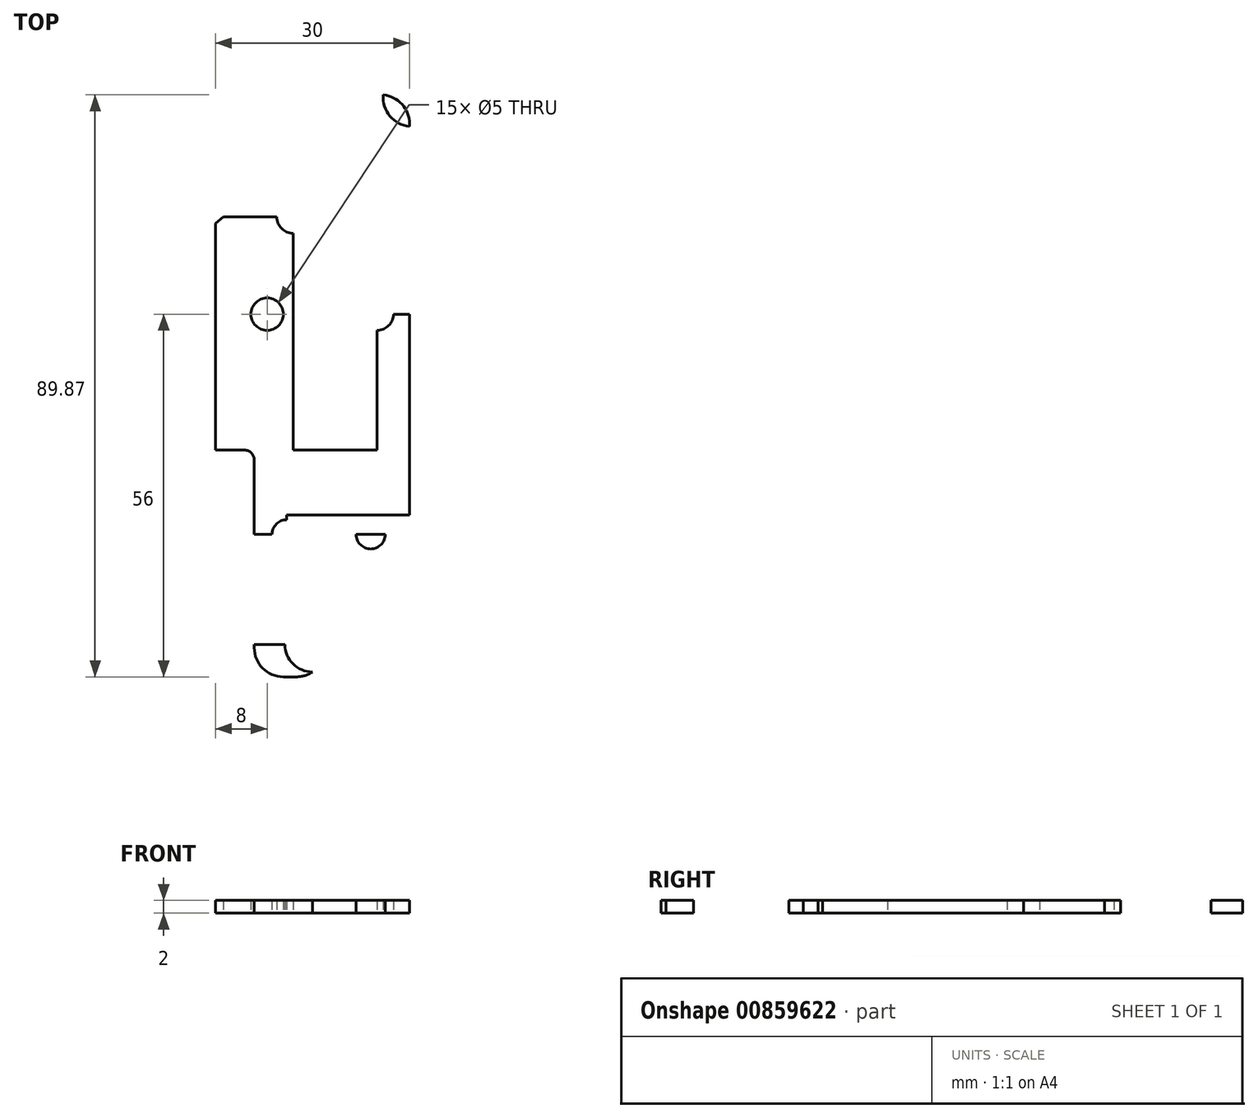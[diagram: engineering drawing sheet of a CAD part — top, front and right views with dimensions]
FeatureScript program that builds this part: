
annotation { "Feature Type Name" : "Feature", "Feature Type Description" : "" }
export const myFeature = defineFeature(function(context is Context, id is Id, definition is map)
    precondition{}
    {
        {
            var Q0;
            Q0=qCreatedBy(makeId("Top.planeOp"),FACE);
            var sketch = newSketch(context, id + "F0", { "sketchPlane" : qUnion([Q0])});
            skLineSegment(sketch, "E0.bottom", {"start": v(12, -12.5) * mm, "end": v(12, 12.5) * mm});
            skLineSegment(sketch, "E0.top", {"start": v(-12, -12.5) * mm, "end": v(-12, 12.5) * mm});
            skLineSegment(sketch, "E0.left", {"start": v(12, -12.5) * mm, "end": v(-12, -12.5) * mm});
            skLineSegment(sketch, "E0.right", {"start": v(12, 12.5) * mm, "end": v(-12, 12.5) * mm});
            skPoint(sketch, "E0.middle", {"position": v(0, 0) * mm});
            skLineSegment(sketch, "E1.bottom", {"start": v(12, 12.5) * mm, "end": v(12, 22.5) * mm});
            skLineSegment(sketch, "E1.top", {"start": v(-12, 12.5) * mm, "end": v(-12, 22.5) * mm});
            skLineSegment(sketch, "E1.right", {"start": v(12, 22.5) * mm, "end": v(-12, 22.5) * mm});
            skLineSegment(sketch, "E2.bottom", {"start": v(12, 22.5) * mm, "end": v(12, 72.5) * mm});
            skLineSegment(sketch, "E2.top", {"start": v(-18, 22.5) * mm, "end": v(-18, 72.5) * mm});
            skLineSegment(sketch, "E2.left", {"start": v(12, 22.5) * mm, "end": v(-18, 22.5) * mm});
            skLineSegment(sketch, "E2.right", {"start": v(12, 72.5) * mm, "end": v(-18, 72.5) * mm});
            skLineSegment(sketch, "E3", {"start": v(-18, 22.5) * mm, "end": v(-18, 57.5) * mm});
            skLineSegment(sketch, "E4", {"start": v(12, 72.5) * mm, "end": v(12, 82.5) * mm});
            skLineSegment(sketch, "E5", {"start": v(12, 82.5) * mm, "end": v(-18, 57.5) * mm});
            skLineSegment(sketch, "E6.bottom", {"start": v(12, 22.5) * mm, "end": v(12, 43.5) * mm});
            skLineSegment(sketch, "E6.top", {"start": v(7, 22.5) * mm, "end": v(7, 43.5) * mm});
            skLineSegment(sketch, "E6.left", {"start": v(12, 22.5) * mm, "end": v(7, 22.5) * mm});
            skLineSegment(sketch, "E6.right", {"start": v(12, 43.5) * mm, "end": v(7, 43.5) * mm});
            skLineSegment(sketch, "E7", {"start": v(7, 43.5) * mm, "end": v(7, 69.5) * mm});
            skCircle(sketch, "E8", {"center": v(7, 69.5) * mm, "radius": 2.5 * mm});
            skCircle(sketch, "E9", {"center": v(7, 43.5) * mm, "radius": 2.5 * mm});
            skLineSegment(sketch, "E10", {"start": v(7, 43.5) * mm, "end": v(-10, 43.5) * mm});
            skCircle(sketch, "E11", {"center": v(-10, 43.5) * mm, "radius": 2.5 * mm});
            skLineSegment(sketch, "E12.bottom", {"start": v(-18, 22.5) * mm, "end": v(-18, 58.5) * mm});
            skLineSegment(sketch, "E12.top", {"start": v(-6, 22.5) * mm, "end": v(-6, 58.5) * mm});
            skLineSegment(sketch, "E12.left", {"start": v(-18, 22.5) * mm, "end": v(-6, 22.5) * mm});
            skLineSegment(sketch, "E12.right", {"start": v(-18, 58.5) * mm, "end": v(-6, 58.5) * mm});
            skCircle(sketch, "E13", {"center": v(-6, 58.5) * mm, "radius": 2.5 * mm});
            skLineSegment(sketch, "E14.bottom", {"start": v(-12, 12.5) * mm, "end": v(-12, 9.5) * mm});
            skLineSegment(sketch, "E14.top", {"start": v(-7, 12.5) * mm, "end": v(-7, 9.5) * mm});
            skLineSegment(sketch, "E14.left", {"start": v(-12, 12.5) * mm, "end": v(-7, 12.5) * mm});
            skLineSegment(sketch, "E14.right", {"start": v(-12, 9.5) * mm, "end": v(-7, 9.5) * mm});
            skCircle(sketch, "E15", {"center": v(-7, 9.5) * mm, "radius": 2.25 * mm});
            skLineSegment(sketch, "E16", {"start": v(12, 9.5) * mm, "end": v(6, 9.5) * mm});
            skCircle(sketch, "E17", {"center": v(6, 9.5) * mm, "radius": 2.25 * mm});
            skLineSegment(sketch, "E18", {"start": v(6, -12.5) * mm, "end": v(6, 1.5) * mm});
            skCircle(sketch, "E19", {"center": v(6, 1.5) * mm, "radius": 3.5 * mm});
            skCircle(sketch, "E20", {"center": v(-7, 1.5) * mm, "radius": 3.5 * mm});
            skPoint(sketch, "E21", {"position": v(-4.75, 9.5) * mm});
            skPoint(sketch, "E22", {"position": v(-9.25, 9.5) * mm});
            skPoint(sketch, "E23", {"position": v(8.25, 9.5) * mm});
            skPoint(sketch, "E24", {"position": v(3.75, 9.5) * mm});
            skLineSegment(sketch, "E25.bottom", {"start": v(8.25, 9.5) * mm, "end": v(8.25, 4.18) * mm});
            skLineSegment(sketch, "E25.top", {"start": v(3.75, 9.5) * mm, "end": v(3.75, 4.18) * mm});
            skLineSegment(sketch, "E25.left", {"start": v(8.25, 9.5) * mm, "end": v(3.75, 9.5) * mm});
            skLineSegment(sketch, "E25.right", {"start": v(8.25, 4.18) * mm, "end": v(3.75, 4.18) * mm});
            skLineSegment(sketch, "E26.bottom", {"start": v(-4.75, 9.5) * mm, "end": v(-4.75, 4.18) * mm});
            skLineSegment(sketch, "E26.top", {"start": v(-9.25, 9.5) * mm, "end": v(-9.25, 4.18) * mm});
            skLineSegment(sketch, "E26.left", {"start": v(-4.75, 9.5) * mm, "end": v(-9.25, 9.5) * mm});
            skLineSegment(sketch, "E26.right", {"start": v(-4.75, 4.18) * mm, "end": v(-9.25, 4.18) * mm});
            skLineSegment(sketch, "E27.bottom", {"start": v(-12, -12.5) * mm, "end": v(-12, -7.5) * mm});
            skLineSegment(sketch, "E27.top", {"start": v(-3, -12.5) * mm, "end": v(-3, -7.5) * mm});
            skLineSegment(sketch, "E27.left", {"start": v(-12, -12.5) * mm, "end": v(-3, -12.5) * mm});
            skLineSegment(sketch, "E27.right", {"start": v(-12, -7.5) * mm, "end": v(-3, -7.5) * mm});
            skCircle(sketch, "E28", {"center": v(-3, -7.5) * mm, "radius": 4.25 * mm});
            skLineSegment(sketch, "E29.bottom", {"start": v(-18, 22.5) * mm, "end": v(-12, 22.5) * mm});
            skLineSegment(sketch, "E29.top", {"start": v(-18, 24) * mm, "end": v(-12, 24) * mm});
            skLineSegment(sketch, "E29.left", {"start": v(-18, 22.5) * mm, "end": v(-18, 24) * mm});
            skLineSegment(sketch, "E29.right", {"start": v(-12, 22.5) * mm, "end": v(-12, 24) * mm});
            skSolve(sketch);
        }
        {
            var Q0;
            {var subQ12=sQuery(id+"F0.wireOp",EDGE,"E2.bottom");Q0=makeQuery(id+"F0.imprint","IMPRINT",FACE,{"disambiguationData":[TD([[makeQuery(id+"F0.imprint","IMPRINT",EDGE,{"derivedFrom":subQ12}),1.0]])]});}
            var Q1;
            Q1=makeQuery(id+"F0.imprint","IMPRINT",FACE,{"disambiguationData":[TD([[makeQuery(id+"F0.imprint","IMPRINT",EDGE,{"derivedFrom":sQuery(id+"F0.wireOp",EDGE,"E11")}),-1.0]])]});
            var Q2;
            {var subQ5=sQuery(id+"F0.wireOp",EDGE,"E2.left");Q2=makeQuery(id+"F0.imprint","IMPRINT",FACE,{"disambiguationData":[TD([[makeQuery(id+"F0.imprint","IMPRINT",EDGE,{"derivedFrom":subQ5}),-1.0]])]});}
            var Q3;
            {var subQ1=sQuery(id+"F0.wireOp",EDGE,"E6.bottom");Q3=makeQuery(id+"F0.imprint","IMPRINT",FACE,{"disambiguationData":[TD([[makeQuery(id+"F0.imprint","IMPRINT",EDGE,{"derivedFrom":subQ1}),1.0]])]});}
            var Q4;
            Q4=makeQuery(id+"F0.imprint","IMPRINT",FACE,{"disambiguationData":[TD([[makeQuery(id+"F0.imprint","IMPRINT",EDGE,{"derivedFrom":sQuery(id+"F0.wireOp",EDGE,"E1.bottom")}),1.0]])]});
            var Q5;
            {var subQ11=sQuery(id+"F0.wireOp",EDGE,"E0.top");Q5=makeQuery(id+"F0.imprint","IMPRINT",FACE,{"disambiguationData":[TD([[makeQuery(id+"F0.imprint","IMPRINT",EDGE,{"derivedFrom":subQ11}),-1.0]])]});}
            var Q6;
            {var subQ0=sQuery(id+"F0.wireOp",EDGE,"E16");Q6=makeQuery(id+"F0.imprint","IMPRINT",FACE,{"disambiguationData":[TD([[makeQuery(id+"F0.imprint","IMPRINT",EDGE,{"derivedFrom":subQ0}),1.0]])]});}
            var Q7;
            {var subQ1=sQuery(id+"F0.wireOp",EDGE,"E27.bottom");Q7=makeQuery(id+"F0.imprint","IMPRINT",FACE,{"disambiguationData":[TD([[makeQuery(id+"F0.imprint","IMPRINT",EDGE,{"derivedFrom":subQ1}),-1.0]])]});}
            var Q8;
            Q8=makeQuery(id+"F0.imprint","IMPRINT",FACE,{"disambiguationData":[TD([[makeQuery(id+"F0.imprint","IMPRINT",EDGE,{"derivedFrom":sQuery(id+"F0.wireOp",EDGE,"E14.bottom")}),1.0]])]});
            var Q9;
            {var subQ0=sQuery(id+"F0.wireOp",EDGE,"E4");Q9=makeQuery(id+"F0.imprint","IMPRINT",FACE,{"disambiguationData":[TD([[makeQuery(id+"F0.imprint","IMPRINT",EDGE,{"derivedFrom":subQ0}),1.0]])]});}
            extrude(context, id + "F1", {"entities" : qUnion([Q0, Q1, Q2, Q3, Q4, Q5, Q6, Q7, Q8, Q9]), "depth" : 2 * mm, "offsetDistance" : 25 * mm});
        }
        {
            var Q0;
            Q0=makeQuery(id+"F1.opExtrude","SWEPT_EDGE",EDGE,{"disambiguationData":[OSD([sQuery(id+"F0.wireOp",EDGE,"E4"),sQuery(id+"F0.wireOp",EDGE,"E5")])]});
            var Q1;
            Q1=makeQuery(id+"F1.opExtrude","SWEPT_EDGE",EDGE,{"disambiguationData":[OSD([sQuery(id+"F0.wireOp",EDGE,"E5"),sQuery(id+"F0.wireOp",EDGE,"E12.bottom")])]});
            var Q2;
            Q2=makeQuery(id+"F1.opExtrude","SWEPT_EDGE",EDGE,{"disambiguationData":[OSD([sQuery(id+"F0.wireOp",EDGE,"E12.bottom"),sQuery(id+"F0.wireOp",EDGE,"E12.left")])]});
            var Q3;
            Q3=makeQuery(id+"F1.opExtrude","SWEPT_EDGE",EDGE,{"disambiguationData":[OSD([sQuery(id+"F0.wireOp",EDGE,"E27.bottom"),sQuery(id+"F0.wireOp",EDGE,"E27.left")])]});
            var Q4;
            Q4=makeQuery(id+"F1.opExtrude","SWEPT_EDGE",EDGE,{"disambiguationData":[OSD([sQuery(id+"F0.wireOp",EDGE,"E0.bottom"),sQuery(id+"F0.wireOp",EDGE,"E0.left")])]});
            var Q5;
            Q5=makeQuery(id+"F1.opExtrude","SWEPT_EDGE",EDGE,{"disambiguationData":[OSD([sQuery(id+"F0.wireOp",EDGE,"E12.bottom"),sQuery(id+"F0.wireOp",EDGE,"E29.top"),sQuery(id+"F0.wireOp",EDGE,"E29.left")])]});
            fillet(context, id + "F2", {"entities" : qUnion([Q0, Q1, Q2, Q3, Q4, Q5]), "radius" : 4.5 * mm, "tangentPropagation" : true, "allowEdgeOverflow" : false});
        }
        {
            var Q0;
            Q0=makeQuery(id+"F1.opExtrude","SWEPT_EDGE",EDGE,{"disambiguationData":[OSD([sQuery(id+"F0.wireOp",EDGE,"E29.top"),sQuery(id+"F0.wireOp",EDGE,"E29.right")])]});
            fillet(context, id + "F3", {"entities" : qUnion([Q0]), "radius" : 1.5 * mm, "tangentPropagation" : true, "allowEdgeOverflow" : false});
        }
    });
